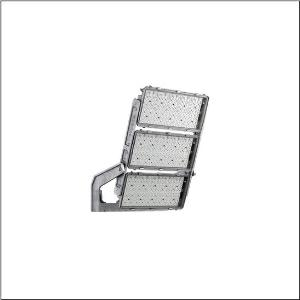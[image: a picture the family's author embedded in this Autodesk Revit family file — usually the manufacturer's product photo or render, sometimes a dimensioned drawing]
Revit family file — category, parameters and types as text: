
# Revit family: floodlight_fl_11_maxi_pro_remote___pl33tblc_5xa779425h01aa_685d
name_source: partatom
category: Lighting Fixtures
units: mm (PartAtom-declared; Revit-internal decimal feet)

## family parameters
Cut with Voids When Loaded = No
Host = Face
Light Source = No
Part Type = Normal
Room Calculation Point = No
Round Connector Dimension = Use Diameter
Shared = No

## types (1)
- --- (1 x LED, 117060 lm, 1335.4 W, 3000K)
    Apparent Load = 1335 VA
    CIE Flux Codes = 24 77 100 100 100
    Color Rendering = 70
    Color Temperature = 3000K
    Default Elevation = 1800 mm
    Description = Floodlight FL 11  maxi  pro Remote floodlight; light control with lens of PMMA; cover panel of toughened safety glass, transparent; light distribution: PL33TBLC, asymmetric direct distribution, LEDcolour temperature: 3000K, rated luminous flux: 117.060lm, colour rendering: CRI > 70, light colour: 730; luminous efficacy: 88lm/W; brightness control: DALI 2 (1 DALI address); with terminal, 8-pole, max. 2.5mm², mains connection: 220..240V/380..400V AC, 50/60Hz, surge voltage resistance: line to ground: 10kV, ECG replaceable separately, LED unit replaceable without ESD environment, dustproof LED module, dimming range 10..100%, no afterglow with DALI off / DMX off command; 1335W floodlight with 2x LED unit of diecast aluminium, coated grey; length: 713mm / width: 651mm / height: 338mm; mounting bracket, of diecast aluminium, uncoated, natural, equipment: Power, protection rating (complete): IP66; insulation class (complete): insulation class I (protective earthing); certification: CE, ENEC, VDE; ball protection: ball impact resistance with accessories, impact resistance: IK07; rated ambient temperature 10°C, only for outdoor installations, permissible operating ambient temperature: -40..+30°C, permissible storage temperature: -40..+85°C; packaging unit: 1 piece

Light Distribution: PL33TBLC
    Height = 320 mm
    Lamp = 1 x LED
    Lamp Light Flux = 117060 lm
    Lamp Power = 1335.4 W
    Lamp count = 1
    Length = 1002 mm
    Luminous efficacy = 88 lm/W
    Manufacturer = Siteco
    ModVariant = No
    Model = 5XA779425H01AA
    Mounting Place = Ceiling
    Mounting Type = Surface mounted
    Number of Poles = 1
    OnlyDefault = Yes
    Power Factor = 1
    Product Name = Floodlight FL 11 maxi pro Remote | PL33TBLC
    Product group = floodlight | ceiling mounted
    ProductGroupID = 303
    Protection Class = Protection class I
    Protection Degree = IP 66
    RLX_Detail_Level = 1
    RLX_Emergency_Light_Flux = 0 lm
    RLX_Emergency_Type = 0
    RLX_Emergency_Type_DB = No
    RlxData = <blob elided: 52273 chars, md5=19f8e9c3>
    Socket = socket
    Standby Power = 0 W
    System Light Flux = 117060 lm
    System Power = 1335 W
    Type Comments = factory setting: luminous flux: 100 % | dim-lin: 254 | 920 mA
    Type Image = l_1006784.jpg
    URL = http://relux.com
    VarID = @adj_044669
    Voltage = 0 V
    Weight = 0.00 kg
    Width = 655 mm

## geometry (parser evidence)
native form markers: Blend x4, Sweep x14
no freeform markers — native parametric forms only
